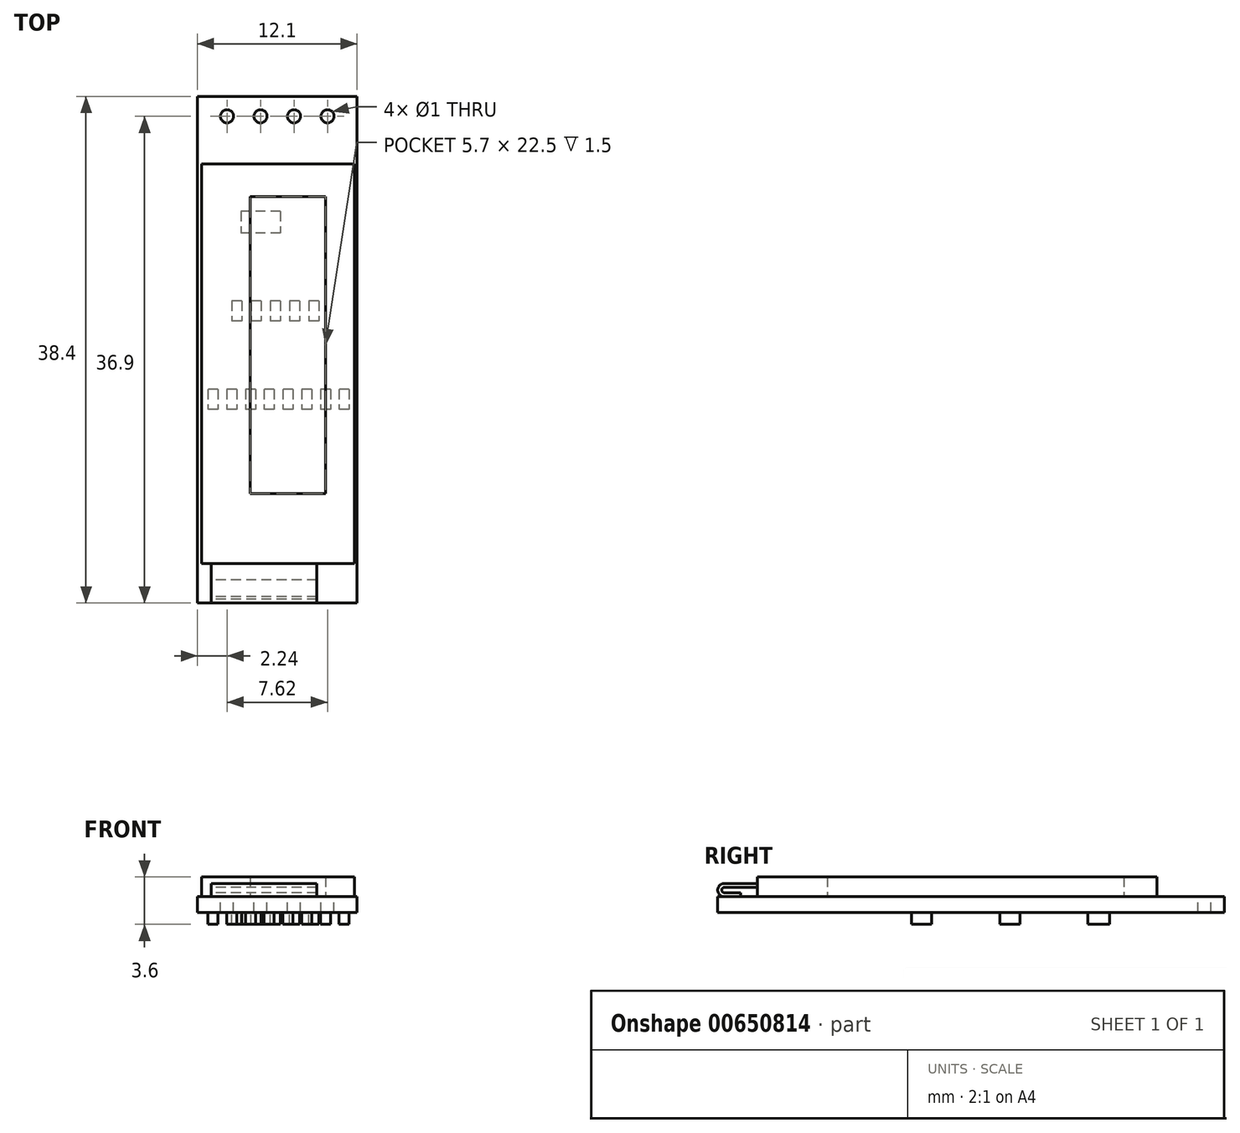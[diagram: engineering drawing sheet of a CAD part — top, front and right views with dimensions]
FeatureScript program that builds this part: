
annotation { "Feature Type Name" : "Feature", "Feature Type Description" : "" }
export const myFeature = defineFeature(function(context is Context, id is Id, definition is map)
    precondition{}
    {
        {
            var Q0;
            Q0=qCreatedBy(makeId("Top.planeOp"),FACE);
            var sketch = newSketch(context, id + "F0", { "sketchPlane" : qUnion([Q0])});
            skLineSegment(sketch, "E0.bottom", {"start": v(6.05, 38.4) * mm, "end": v(-6.05, 38.4) * mm});
            skLineSegment(sketch, "E0.left", {"start": v(6.05, 38.4) * mm, "end": v(6.05, 0) * mm});
            skLineSegment(sketch, "E0.right", {"start": v(-6.05, 38.4) * mm, "end": v(-6.05, 0) * mm});
            skPoint(sketch, "E0.middle", {"position": v(0, 19.2) * mm});
            skLineSegment(sketch, "E1", {"start": v(-6.05, 0) * mm, "end": v(6.05, 0) * mm});
            skPoint(sketch, "E2", {"position": v(0, 0) * mm});
            skCircle(sketch, "E3", {"center": v(3.8, 36.9) * mm, "radius": 0.5 * mm});
            skCircle(sketch, "E4.1.0.0", {"center": v(1.27, 36.9) * mm, "radius": 0.5 * mm});
            skCircle(sketch, "E4.2.0.0", {"center": v(-1.27, 36.9) * mm, "radius": 0.5 * mm});
            skCircle(sketch, "E4.3.0.0", {"center": v(-3.81, 36.9) * mm, "radius": 0.5 * mm});
            skLineSegment(sketch, "E4.direction1", {"start": v(3.8, 36.9) * mm, "end": v(1.27, 36.9) * mm, "construction": true});
            skSolve(sketch);
        }
        {
            var Q0;
            Q0=makeQuery(id+"F0.imprint","IMPRINT",FACE,{"disambiguationData":[TD([[makeQuery(id+"F0.imprint","IMPRINT",EDGE,{"derivedFrom":sQuery(id+"F0.wireOp",EDGE,"E0.bottom")}),1.0]])]});
            extrude(context, id + "F1", {"entities" : qUnion([Q0]), "oppositeDirection" : true, "depth" : 1.2 * mm, "offsetDistance" : 25 * mm});
        }
        {
            var Q0;
            Q0=qCreatedBy(makeId("Top.planeOp"),FACE);
            var sketch = newSketch(context, id + "F2", { "sketchPlane" : qUnion([Q0])});
            skLineSegment(sketch, "E5.bottom", {"start": v(-5.75, 33.3) * mm, "end": v(5.85, 33.3) * mm});
            skLineSegment(sketch, "E5.top", {"start": v(-5.75, 3) * mm, "end": v(5.85, 3) * mm});
            skLineSegment(sketch, "E5.left", {"start": v(-5.75, 33.3) * mm, "end": v(-5.75, 3) * mm});
            skLineSegment(sketch, "E5.right", {"start": v(5.85, 33.3) * mm, "end": v(5.85, 3) * mm});
            skPoint(sketch, "E5.middle", {"position": v(0.05, 18.15) * mm});
            skLineSegment(sketch, "E6.bottom", {"start": v(3.65, 30.8) * mm, "end": v(-2.05, 30.8) * mm});
            skLineSegment(sketch, "E6.top", {"start": v(3.65, 8.3) * mm, "end": v(-2.05, 8.3) * mm});
            skLineSegment(sketch, "E6.left", {"start": v(3.65, 30.8) * mm, "end": v(3.65, 8.3) * mm});
            skLineSegment(sketch, "E6.right", {"start": v(-2.05, 30.8) * mm, "end": v(-2.05, 8.3) * mm});
            skPoint(sketch, "E6.middle", {"position": v(0.8, 19.55) * mm});
            skSolve(sketch);
        }
        {
            var Q0;
            Q0=makeQuery(id+"F2.imprint","IMPRINT",FACE,{"disambiguationData":[TD([[makeQuery(id+"F2.imprint","IMPRINT",EDGE,{"derivedFrom":sQuery(id+"F2.wireOp",EDGE,"E5.bottom")}),-1.0]])]});
            extrude(context, id + "F3", {"entities" : qUnion([Q0]), "depth" : 1.5 * mm, "offsetDistance" : 25 * mm});
        }
        {
            var Q0;
            Q0=makeQuery(id+"F2.imprint","IMPRINT",FACE,{"disambiguationData":[TD([[makeQuery(id+"F2.imprint","IMPRINT",EDGE,{"derivedFrom":sQuery(id+"F2.wireOp",EDGE,"E6.bottom")}),1.0]])]});
            var Q1;
            Q1=makeQuery(id+"F3.opExtrude","CAP_FACE",FACE,{"disambiguationData":[OSD([sQuery(id+"F2.wireOp",EDGE,"E5.bottom"),sQuery(id+"F2.wireOp",EDGE,"E5.top"),sQuery(id+"F2.wireOp",EDGE,"E5.left"),sQuery(id+"F2.wireOp",EDGE,"E5.right"),sQuery(id+"F2.wireOp",EDGE,"E6.bottom"),sQuery(id+"F2.wireOp",EDGE,"E6.top"),sQuery(id+"F2.wireOp",EDGE,"E6.left"),sQuery(id+"F2.wireOp",EDGE,"E6.right")])],"isStart":false});
            extrude(context, id + "F4", {"entities" : qUnion([Q0]), "endBound" : BoundingType.UP_TO_SURFACE, "depth" : 25 * mm, "endBoundEntityFace" : qUnion([Q1]), "offsetDistance" : 25 * mm});
        }
        {
            var Q0;
            Q0=qCreatedBy(makeId("Right.planeOp"),FACE);
            var sketch = newSketch(context, id + "F5", { "sketchPlane" : qUnion([Q0])});
            skArc(sketch, "E7", {"start": v(0.5, 1) * mm, "mid": v(0, 0.5) * mm, "end": v(0.5, 0) * mm});
            skLineSegment(sketch, "E8", {"start": v(0.5, 0) * mm, "end": v(1.75, 0) * mm});
            skLineSegment(sketch, "E9", {"start": v(0.5, 1) * mm, "end": v(3, 1) * mm});
            skLineSegment(sketch, "E10", {"start": v(3, 1) * mm, "end": v(3, 0.7) * mm});
            skLineSegment(sketch, "E11", {"start": v(1.75, 0.3) * mm, "end": v(1.75, 0) * mm});
            skArc(sketch, "E12", {"start": v(0.5, 0.3) * mm, "mid": v(0.3, 0.5) * mm, "end": v(0.5, 0.7) * mm});
            skLineSegment(sketch, "E13", {"start": v(0.5, 0.7) * mm, "end": v(3, 0.7) * mm});
            skLineSegment(sketch, "E14", {"start": v(0.5, 0.3) * mm, "end": v(1.75, 0.3) * mm});
            skSolve(sketch);
        }
        {
            var Q0;
            Q0=makeQuery(id+"F5.imprint","IMPRINT",FACE,{"disambiguationData":[TD([[makeQuery(id+"F5.imprint","IMPRINT",EDGE,{"derivedFrom":sQuery(id+"F5.wireOp",EDGE,"E7")}),1.0]])]});
            extrude(context, id + "F6", {"entities" : qUnion([Q0]), "operationType" : NewBodyOperationType.ADD, "depth" : 3 * mm, "offsetDistance" : 25 * mm, "hasSecondDirection" : true, "secondDirectionOppositeDirection" : true, "secondDirectionDepth" : 5 * mm});
        }
        {
            var Q0;
            Q0=makeQuery(id+"F1.opExtrude","CAP_FACE",FACE,{"disambiguationData":[OSD([sQuery(id+"F0.wireOp",EDGE,"E0.bottom"),sQuery(id+"F0.wireOp",EDGE,"E0.top"),sQuery(id+"F0.wireOp",EDGE,"E0.left"),sQuery(id+"F0.wireOp",EDGE,"E0.right"),sQuery(id+"F0.wireOp",EDGE,"E1"),sQuery(id+"F0.wireOp",EDGE,"aDX1qpH9-lFEn-ixr9-Dufl-y7F3YnxQyYci"),sQuery(id+"F0.wireOp",EDGE,"gvd0Yhti-X2SK-3slb-J16A-NT5B4LvoGFiH"),sQuery(id+"F0.wireOp",EDGE,"fc18eb17-40c7-4a79-aced-eae2537e06b1.trimOffspring"),sQuery(id+"F0.wireOp",EDGE,"HQJKGbPS-CtYr-E5al-H3nJ-FSlFHONFvJQt"),sQuery(id+"F0.wireOp",EDGE,"nHQG2h4k-9CPI-FnFt-DvPW-ehateDD3xt6G"),sQuery(id+"F0.wireOp",EDGE,"ZTteRkPn-eDy3-4HKR-dk3l-BrD2dNXCBh6q"),sQuery(id+"F0.wireOp",EDGE,"D5cmBYIi-BP5q-sfKf-TnSp-QLMnZgETNZnF"),sQuery(id+"F0.wireOp",EDGE,"E3"),sQuery(id+"F0.wireOp",EDGE,"E4.1.0.0"),sQuery(id+"F0.wireOp",EDGE,"E4.2.0.0"),sQuery(id+"F0.wireOp",EDGE,"E4.3.0.0")])],"isStart":false});
            var sketch = newSketch(context, id + "F7", { "sketchPlane" : qUnion([Q0])});
            skLineSegment(sketch, "E15.bottom", {"start": v(5.45, -16.2) * mm, "end": v(4.69, -16.2) * mm});
            skLineSegment(sketch, "E15.top", {"start": v(5.45, -14.68) * mm, "end": v(4.69, -14.68) * mm});
            skLineSegment(sketch, "E15.left", {"start": v(5.45, -16.2) * mm, "end": v(5.45, -14.68) * mm});
            skLineSegment(sketch, "E15.right", {"start": v(4.69, -16.2) * mm, "end": v(4.69, -14.68) * mm});
            skLineSegment(sketch, "E16.1.0.0", {"start": v(3.27, -16.2) * mm, "end": v(3.27, -14.68) * mm});
            skLineSegment(sketch, "E16.1.0.1", {"start": v(4.03, -16.2) * mm, "end": v(3.27, -16.2) * mm});
            skLineSegment(sketch, "E16.1.0.2", {"start": v(4.03, -16.2) * mm, "end": v(4.03, -14.68) * mm});
            skLineSegment(sketch, "E16.1.0.3", {"start": v(4.03, -14.68) * mm, "end": v(3.27, -14.68) * mm});
            skLineSegment(sketch, "E16.2.0.0", {"start": v(1.85, -16.2) * mm, "end": v(1.85, -14.68) * mm});
            skLineSegment(sketch, "E16.2.0.1", {"start": v(2.61, -16.2) * mm, "end": v(1.85, -16.2) * mm});
            skLineSegment(sketch, "E16.2.0.2", {"start": v(2.61, -16.2) * mm, "end": v(2.61, -14.68) * mm});
            skLineSegment(sketch, "E16.2.0.3", {"start": v(2.61, -14.68) * mm, "end": v(1.85, -14.68) * mm});
            skLineSegment(sketch, "E16.3.0.0", {"start": v(0.43, -16.2) * mm, "end": v(0.43, -14.68) * mm});
            skLineSegment(sketch, "E16.3.0.1", {"start": v(1.2, -16.2) * mm, "end": v(0.43, -16.2) * mm});
            skLineSegment(sketch, "E16.3.0.2", {"start": v(1.2, -16.2) * mm, "end": v(1.2, -14.68) * mm});
            skLineSegment(sketch, "E16.3.0.3", {"start": v(1.2, -14.68) * mm, "end": v(0.43, -14.68) * mm});
            skLineSegment(sketch, "E16.4.0.0", {"start": v(-1, -16.2) * mm, "end": v(-1, -14.68) * mm});
            skLineSegment(sketch, "E16.4.0.1", {"start": v(-0.23, -16.2) * mm, "end": v(-1, -16.2) * mm});
            skLineSegment(sketch, "E16.4.0.2", {"start": v(-0.23, -16.2) * mm, "end": v(-0.23, -14.68) * mm});
            skLineSegment(sketch, "E16.4.0.3", {"start": v(-0.23, -14.68) * mm, "end": v(-1, -14.68) * mm});
            skLineSegment(sketch, "E16.5.0.0", {"start": v(-2.41, -16.2) * mm, "end": v(-2.41, -14.68) * mm});
            skLineSegment(sketch, "E16.5.0.1", {"start": v(-1.65, -16.2) * mm, "end": v(-2.41, -16.2) * mm});
            skLineSegment(sketch, "E16.5.0.2", {"start": v(-1.65, -16.2) * mm, "end": v(-1.65, -14.68) * mm});
            skLineSegment(sketch, "E16.5.0.3", {"start": v(-1.65, -14.68) * mm, "end": v(-2.41, -14.68) * mm});
            skLineSegment(sketch, "E16.direction1", {"start": v(4.69, -16.2) * mm, "end": v(3.27, -16.2) * mm, "construction": true});
            skLineSegment(sketch, "E17.bottom", {"start": v(0.25, -29.7) * mm, "end": v(-2.75, -29.7) * mm});
            skLineSegment(sketch, "E17.top", {"start": v(0.25, -28.05) * mm, "end": v(-2.75, -28.05) * mm});
            skLineSegment(sketch, "E17.left", {"start": v(0.25, -29.7) * mm, "end": v(0.25, -28.05) * mm});
            skLineSegment(sketch, "E17.right", {"start": v(-2.75, -29.7) * mm, "end": v(-2.75, -28.05) * mm});
            skLineSegment(sketch, "E18.0.6.0", {"start": v(-3.83, -16.2) * mm, "end": v(-3.83, -14.68) * mm});
            skLineSegment(sketch, "E18.3.6.0", {"start": v(-3.07, -16.2) * mm, "end": v(-3.83, -16.2) * mm});
            skLineSegment(sketch, "E18.6.6.0", {"start": v(-3.07, -16.2) * mm, "end": v(-3.07, -14.68) * mm});
            skLineSegment(sketch, "E18.9.6.0", {"start": v(-3.07, -14.68) * mm, "end": v(-3.83, -14.68) * mm});
            skLineSegment(sketch, "E18.0.7.0", {"start": v(-5.25, -16.2) * mm, "end": v(-5.25, -14.68) * mm});
            skLineSegment(sketch, "E18.3.7.0", {"start": v(-4.49, -16.2) * mm, "end": v(-5.25, -16.2) * mm});
            skLineSegment(sketch, "E18.6.7.0", {"start": v(-4.49, -16.2) * mm, "end": v(-4.49, -14.68) * mm});
            skLineSegment(sketch, "E18.9.7.0", {"start": v(-4.49, -14.68) * mm, "end": v(-5.25, -14.68) * mm});
            skLineSegment(sketch, "E19.bottom", {"start": v(3.15, -22.9) * mm, "end": v(2.39, -22.9) * mm});
            skLineSegment(sketch, "E19.top", {"start": v(3.15, -21.38) * mm, "end": v(2.39, -21.38) * mm});
            skLineSegment(sketch, "E19.left", {"start": v(3.15, -22.9) * mm, "end": v(3.15, -21.38) * mm});
            skLineSegment(sketch, "E19.right", {"start": v(2.39, -22.9) * mm, "end": v(2.39, -21.38) * mm});
            skLineSegment(sketch, "E20.1.0.0", {"start": v(1.7, -22.9) * mm, "end": v(0.93, -22.9) * mm});
            skLineSegment(sketch, "E20.1.0.1", {"start": v(1.7, -21.38) * mm, "end": v(0.93, -21.38) * mm});
            skLineSegment(sketch, "E20.1.0.2", {"start": v(0.93, -22.9) * mm, "end": v(0.93, -21.38) * mm});
            skLineSegment(sketch, "E20.1.0.3", {"start": v(1.7, -22.9) * mm, "end": v(1.7, -21.38) * mm});
            skLineSegment(sketch, "E20.2.0.0", {"start": v(0.23, -22.9) * mm, "end": v(-0.53, -22.9) * mm});
            skLineSegment(sketch, "E20.2.0.1", {"start": v(0.23, -21.38) * mm, "end": v(-0.53, -21.38) * mm});
            skLineSegment(sketch, "E20.2.0.2", {"start": v(-0.53, -22.9) * mm, "end": v(-0.53, -21.38) * mm});
            skLineSegment(sketch, "E20.2.0.3", {"start": v(0.23, -22.9) * mm, "end": v(0.23, -21.38) * mm});
            skLineSegment(sketch, "E20.3.0.0", {"start": v(-1.23, -22.9) * mm, "end": v(-2, -22.9) * mm});
            skLineSegment(sketch, "E20.3.0.1", {"start": v(-1.23, -21.38) * mm, "end": v(-2, -21.38) * mm});
            skLineSegment(sketch, "E20.3.0.2", {"start": v(-2, -22.9) * mm, "end": v(-2, -21.38) * mm});
            skLineSegment(sketch, "E20.3.0.3", {"start": v(-1.23, -22.9) * mm, "end": v(-1.23, -21.38) * mm});
            skLineSegment(sketch, "E20.direction1", {"start": v(2.39, -22.9) * mm, "end": v(0.93, -22.9) * mm, "construction": true});
            skLineSegment(sketch, "E21.0.4.0", {"start": v(-2.69, -22.9) * mm, "end": v(-3.45, -22.9) * mm});
            skLineSegment(sketch, "E21.3.4.0", {"start": v(-2.69, -21.38) * mm, "end": v(-3.45, -21.38) * mm});
            skLineSegment(sketch, "E21.6.4.0", {"start": v(-3.45, -22.9) * mm, "end": v(-3.45, -21.38) * mm});
            skLineSegment(sketch, "E21.9.4.0", {"start": v(-2.69, -22.9) * mm, "end": v(-2.69, -21.38) * mm});
            skSolve(sketch);
        }
        {
            var Q0;
            Q0=qSketchRegion(id+"F7",true);
            extrude(context, id + "F8", {"entities" : qUnion([Q0]), "operationType" : NewBodyOperationType.ADD, "depth" : 0.9 * mm, "offsetDistance" : 25 * mm});
        }
    });
